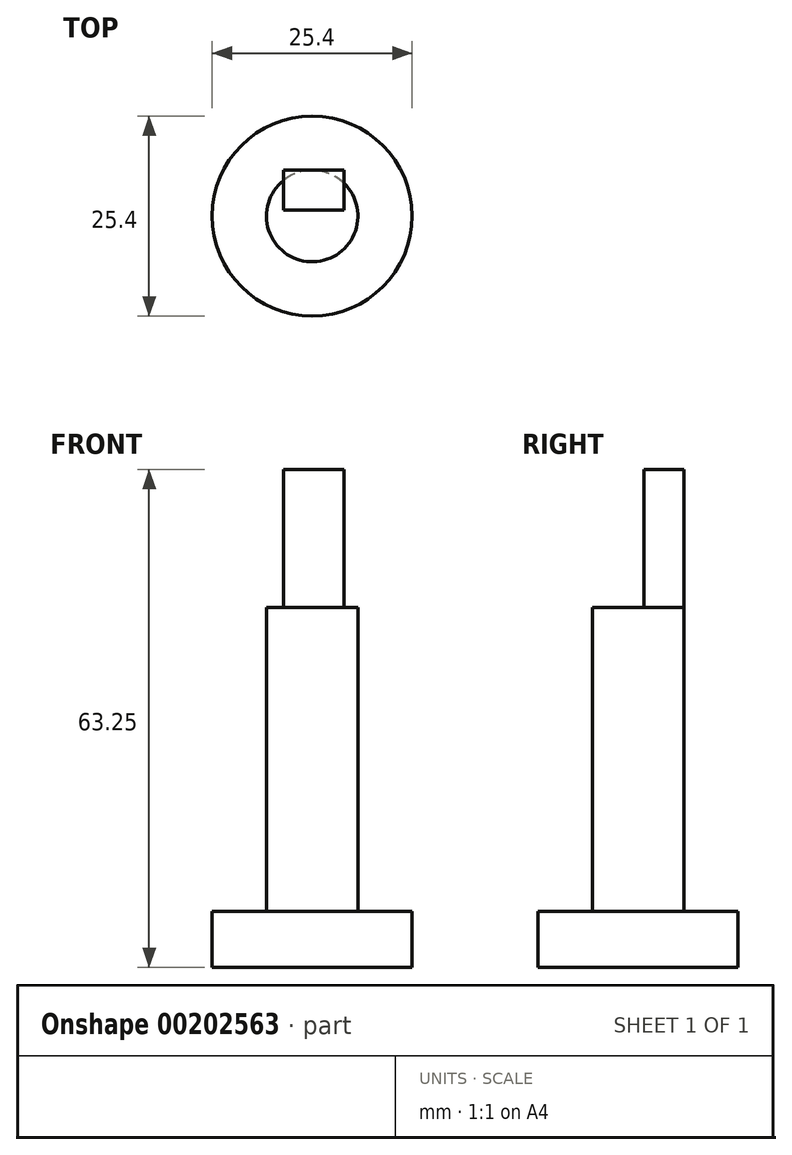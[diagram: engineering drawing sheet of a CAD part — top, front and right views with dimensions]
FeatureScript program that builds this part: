
annotation { "Feature Type Name" : "Feature", "Feature Type Description" : "" }
export const myFeature = defineFeature(function(context is Context, id is Id, definition is map)
    precondition{}
    {
        {
            var Q0;
            Q0=qCreatedBy(makeId("Top.planeOp"),FACE);
            var sketch = newSketch(context, id + "F0", { "sketchPlane" : qUnion([Q0])});
            skCircle(sketch, "E0", {"center": v(0, 0) * mm, "radius": 12.7 * mm});
            skSolve(sketch);
        }
        {
            var Q0;
            Q0=makeQuery(id+"F0.imprint","IMPRINT",FACE,{"disambiguationData":[TD([[makeQuery(id+"F0.imprint","IMPRINT",EDGE,{"derivedFrom":sQuery(id+"F0.wireOp",EDGE,"E0")}),1.0]])]});
            extrude(context, id + "F1", {"entities" : qUnion([Q0]), "depth" : 7.11 * mm});
        }
        {
            var Q0;
            Q0=makeQuery(id+"F1.opExtrude","CAP_FACE",FACE,{"disambiguationData":[OSD([sQuery(id+"F0.wireOp",EDGE,"E0")])],"isStart":false});
            var sketch = newSketch(context, id + "F2", { "sketchPlane" : qUnion([Q0])});
            skCircle(sketch, "E1", {"center": v(0, 0) * mm, "radius": 5.81 * mm});
            skSolve(sketch);
        }
        {
            var Q0;
            Q0=makeQuery(id+"F2.imprint","IMPRINT",FACE,{"disambiguationData":[TD([[makeQuery(id+"F2.imprint","IMPRINT",EDGE,{"derivedFrom":sQuery(id+"F2.wireOp",EDGE,"E1")}),1.0]])]});
            extrude(context, id + "F3", {"entities" : qUnion([Q0]), "operationType" : NewBodyOperationType.ADD, "depth" : 38.6 * mm});
        }
        {
            var Q0;
            Q0=makeQuery(id+"F3.opExtrude","CAP_FACE",FACE,{"disambiguationData":[OSD([sQuery(id+"F2.wireOp",EDGE,"E1")])],"isStart":false});
            var sketch = newSketch(context, id + "F4", { "sketchPlane" : qUnion([Q0])});
            skLineSegment(sketch, "E2.bottom", {"start": v(4.04, 5.81) * mm, "end": v(-3.64, 5.81) * mm});
            skLineSegment(sketch, "E2.top", {"start": v(4.04, 0.73) * mm, "end": v(-3.64, 0.73) * mm});
            skLineSegment(sketch, "E2.left", {"start": v(4.04, 5.81) * mm, "end": v(4.04, 0.73) * mm});
            skLineSegment(sketch, "E2.right", {"start": v(-3.64, 5.81) * mm, "end": v(-3.64, 0.73) * mm});
            skSolve(sketch);
        }
        {
            var Q0;
            {var subQ5=sQuery(id+"F4.wireOp",EDGE,"E2.top");Q0=makeQuery(id+"F4.imprint","IMPRINT",FACE,{"disambiguationData":[TD([[makeQuery(id+"F4.imprint","IMPRINT",EDGE,{"derivedFrom":subQ5}),-1.0]])]});}
            var Q1;
            {var subQ0=sQuery(id+"F4.wireOp",EDGE,"E2.right");var subQ1=sQuery(id+"F4.wireOp",EDGE,"E2.bottom");var subQ2=makeQuery(id+"F4.imprint","INTERSECT",VERTEX,{"derivedFrom":[subQ1,subQ0]});Q1=makeQuery(id+"F4.imprint","IMPRINT",FACE,{"disambiguationData":[TD([[makeQuery(id+"F4.imprint","IMPRINT",EDGE,{"disambiguationData":[TD([[subQ2,1.0]])],"derivedFrom":subQ1}),1.0]])]});}
            var Q2;
            {var subQ0=sQuery(id+"F4.wireOp",EDGE,"E2.left");var subQ1=sQuery(id+"F4.wireOp",EDGE,"E2.bottom");var subQ2=makeQuery(id+"F4.imprint","INTERSECT",VERTEX,{"derivedFrom":[subQ1,subQ0]});Q2=makeQuery(id+"F4.imprint","IMPRINT",FACE,{"disambiguationData":[TD([[makeQuery(id+"F4.imprint","IMPRINT",EDGE,{"disambiguationData":[TD([[subQ2,-1.0]])],"derivedFrom":subQ1}),1.0]])]});}
            extrude(context, id + "F5", {"entities" : qUnion([Q0, Q1, Q2]), "operationType" : NewBodyOperationType.ADD, "depth" : 17.53 * mm});
        }
    });
